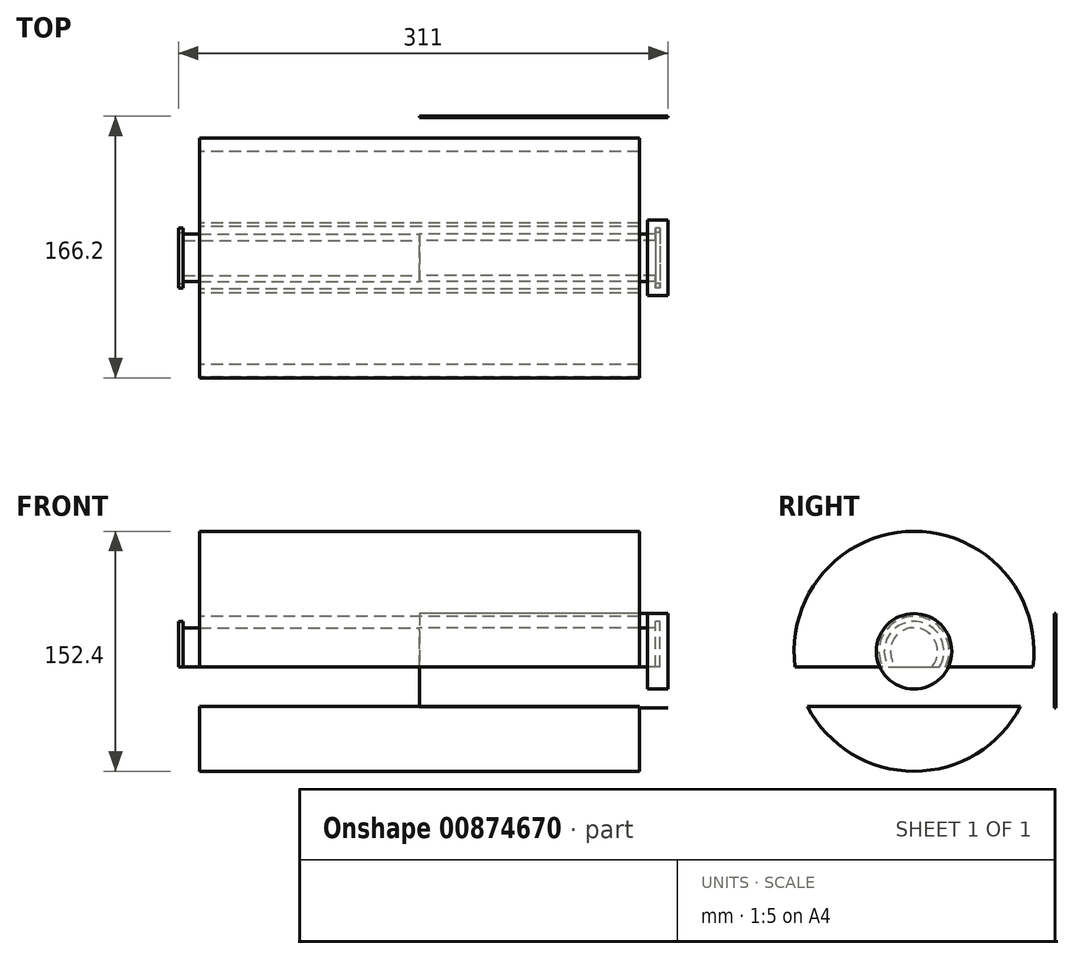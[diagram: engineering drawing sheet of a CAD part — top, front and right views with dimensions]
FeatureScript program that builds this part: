
annotation { "Feature Type Name" : "Feature", "Feature Type Description" : "" }
export const myFeature = defineFeature(function(context is Context, id is Id, definition is map)
    precondition{}
    {
        {
            var Q0;
            Q0=qCreatedBy(makeId("Right.planeOp"),FACE);
            var sketch = newSketch(context, id + "F0", { "sketchPlane" : qUnion([Q0])});
            skCircle(sketch, "E0", {"center": v(0, 0) * mm, "radius": 76.2 * mm});
            skCircle(sketch, "E1", {"center": v(0, 0) * mm, "radius": 22.23 * mm});
            skCircle(sketch, "E2", {"center": v(0, 0) * mm, "radius": 15 * mm});
            skCircle(sketch, "E3", {"center": v(0, 0) * mm, "radius": 19 * mm});
            skPoint(sketch, "E4", {"position": v(-19, 0) * mm});
            skPoint(sketch, "E5", {"position": v(-15, 0) * mm});
            skPoint(sketch, "E6", {"position": v(-22.23, 0) * mm});
            skPoint(sketch, "E7", {"position": v(15, 0) * mm});
            skPoint(sketch, "E8", {"position": v(19, 0) * mm});
            skPoint(sketch, "E9", {"position": v(22.23, 0) * mm});
            skPoint(sketch, "E10", {"position": v(0, 15) * mm});
            skPoint(sketch, "E11", {"position": v(0, 19) * mm});
            skPoint(sketch, "E12", {"position": v(0, 22.23) * mm});
            skPoint(sketch, "E13", {"position": v(0, -15) * mm});
            skPoint(sketch, "E14", {"position": v(0, -19) * mm});
            skPoint(sketch, "E15", {"position": v(0, -22.23) * mm});
            skSolve(sketch);
        }
        {
            var Q0;
            Q0=makeQuery(id+"F0.imprint","IMPRINT",FACE,{"disambiguationData":[TD([[makeQuery(id+"F0.imprint","IMPRINT",EDGE,{"derivedFrom":sQuery(id+"F0.wireOp",EDGE,"E0")}),1.0]])]});
            extrude(context, id + "F1", {"entities" : qUnion([Q0]), "endBound" : BoundingType.SYMMETRIC, "depth" : 279.4 * mm, "offsetDistance" : 25 * mm});
        }
        {
            var Q0;
            Q0=makeQuery(id+"F0.imprint","IMPRINT",FACE,{"disambiguationData":[TD([[makeQuery(id+"F0.imprint","IMPRINT",EDGE,{"derivedFrom":sQuery(id+"F0.wireOp",EDGE,"E2")}),1.0]])]});
            extrude(context, id + "F2", {"entities" : qUnion([Q0]), "depth" : 150 * mm, "offsetDistance" : 25 * mm});
        }
        {
            var Q0;
            Q0=makeQuery(id+"F0.imprint","IMPRINT",FACE,{"disambiguationData":[TD([[makeQuery(id+"F0.imprint","IMPRINT",EDGE,{"derivedFrom":sQuery(id+"F0.wireOp",EDGE,"E2")}),-1.0]])]});
            var Q1;
            Q1=makeQuery(id+"F0.imprint","IMPRINT",FACE,{"disambiguationData":[TD([[makeQuery(id+"F0.imprint","IMPRINT",EDGE,{"derivedFrom":sQuery(id+"F0.wireOp",EDGE,"E2")}),1.0]])]});
            var Q2;
            Q2=makeQuery(id+"F2.opExtrude","CAP_FACE",FACE,{"disambiguationData":[OSD([sQuery(id+"F0.wireOp",EDGE,"E2")])],"isStart":false});
            var Q3;
            Q3=makeQuery(id+"F2.opExtrude","CAP_FACE",FACE,{"disambiguationData":[OSD([sQuery(id+"F0.wireOp",EDGE,"E2")])],"isStart":false});
            extrude(context, id + "F3", {"entities" : qUnion([Q0, Q1]), "operationType" : NewBodyOperationType.ADD, "endBound" : BoundingType.UP_TO_SURFACE, "depth" : 25 * mm, "endBoundEntityFace" : qUnion([Q2]), "hasOffset" : true, "offsetDistance" : 3 * mm, "offsetOppositeDirection" : true, "hasSecondDirection" : true, "secondDirectionBound" : SecondDirectionBoundingType.UP_TO_SURFACE, "secondDirectionOppositeDirection" : false, "secondDirectionDepth" : 25 * mm, "secondDirectionBoundEntityFace" : qUnion([Q3])});
        }
        {
            var Q0;
            Q0=makeQuery(id+"F2.opExtrude","SWEPT_BODY",BODY,{"disambiguationData":[OSD([sQuery(id+"F0.wireOp",EDGE,"E2")])]});
            var Q1;
            Q1=makeQuery(id+"F0.imprint","IMPRINT",FACE,{"disambiguationData":[TD([[makeQuery(id+"F0.imprint","IMPRINT",EDGE,{"derivedFrom":sQuery(id+"F0.wireOp",EDGE,"E2")}),1.0]])]});
            mirror(context, id + "F4", {"operationType" : NewBodyOperationType.ADD, "entities" : qUnion([Q0]), "mirrorPlane" : qUnion([Q1])});
        }
        {
            var Q0;
            Q0=qCreatedBy(makeId("Top.planeOp"),FACE);
            cPlane(context, id + "F5", {"entities" : qUnion([Q0]), "cplaneType" : CPlaneType.OFFSET, "offset" : 10 * mm, "oppositeDirection" : true, "width" : 150 * mm, "height" : 150 * mm});
        }
        {
            var Q0;
            Q0=qCreatedBy(id+"F5.planeOp",FACE);
            var sketch = newSketch(context, id + "F6", { "sketchPlane" : qUnion([Q0])});
            skLineSegment(sketch, "E16.bottom", {"start": v(215.89, -121.03) * mm, "end": v(-215.89, -121.03) * mm});
            skLineSegment(sketch, "E16.top", {"start": v(215.89, 160.12) * mm, "end": v(-215.89, 160.12) * mm});
            skLineSegment(sketch, "E16.left", {"start": v(215.89, -121.03) * mm, "end": v(215.89, 160.12) * mm});
            skLineSegment(sketch, "E16.right", {"start": v(-215.89, -121.03) * mm, "end": v(-215.89, 160.12) * mm});
            skPoint(sketch, "E16.middle", {"position": v(0, 19.54) * mm});
            skSolve(sketch);
        }
        {
            var Q0;
            Q0=makeQuery(id+"F6.imprint","IMPRINT",FACE,{"disambiguationData":[TD([[makeQuery(id+"F6.imprint","IMPRINT",EDGE,{"derivedFrom":sQuery(id+"F6.wireOp",EDGE,"E16.bottom")}),-1.0]])]});
            extrude(context, id + "F7", {"entities" : qUnion([Q0]), "operationType" : NewBodyOperationType.REMOVE, "oppositeDirection" : true, "depth" : 25 * mm, "offsetDistance" : 25 * mm});
        }
        {
            var Q0;
            Q0=qCreatedBy(makeId("Front.planeOp"),FACE);
            cPlane(context, id + "F8", {"entities" : qUnion([Q0]), "cplaneType" : CPlaneType.OFFSET, "offset" : 90 * mm, "oppositeDirection" : true, "width" : 150 * mm, "height" : 150 * mm});
        }
        {
            var Q0;
            Q0=qCreatedBy(id+"F8.planeOp",FACE);
            var sketch = newSketch(context, id + "F9", { "sketchPlane" : qUnion([Q0])});
            skLineSegment(sketch, "E17", {"start": v(150, 19) * mm, "end": v(153, 19) * mm});
            skLineSegment(sketch, "E18.0", {"start": v(153, -10) * mm, "end": v(150, -10) * mm});
            skLineSegment(sketch, "E19.0", {"start": v(150, -10) * mm, "end": v(150, 19) * mm});
            skLineSegment(sketch, "E20.0", {"start": v(153, -10) * mm, "end": v(153, 19) * mm});
            skLineSegment(sketch, "E21.bottom", {"start": v(158, 24) * mm, "end": v(0, 24) * mm});
            skLineSegment(sketch, "E21.top", {"start": v(158, -36) * mm, "end": v(0, -36) * mm});
            skLineSegment(sketch, "E21.left", {"start": v(158, 24) * mm, "end": v(158, -36) * mm});
            skPoint(sketch, "E22", {"position": v(0, 24) * mm});
            skPoint(sketch, "E23.orphan", {"position": v(-158, 24) * mm});
            skPoint(sketch, "E24.end.orphan", {"position": v(-158, -36) * mm});
            skLineSegment(sketch, "E25", {"start": v(0, 24) * mm, "end": v(0, -36) * mm});
            skLineSegment(sketch, "E26", {"start": v(145, 24) * mm, "end": v(145, -36) * mm});
            skSolve(sketch);
        }
        {
            var Q0;
            Q0=makeQuery(id+"F9.imprint","IMPRINT",FACE,{"disambiguationData":[TD([[makeQuery(id+"F9.imprint","IMPRINT",EDGE,{"derivedFrom":sQuery(id+"F9.wireOp",EDGE,"E17")}),1.0]])]});
            var Q1;
            Q1=makeQuery(id+"F9.imprint","IMPRINT",FACE,{"disambiguationData":[TD([[makeQuery(id+"F9.imprint","IMPRINT",EDGE,{"derivedFrom":sQuery(id+"F9.wireOp",EDGE,"E17")}),-1.0]])]});
            var Q2;
            {var subQ0=sQuery(id+"F9.wireOp",EDGE,"E25");Q2=makeQuery(id+"F9.imprint","IMPRINT",FACE,{"disambiguationData":[TD([[makeQuery(id+"F9.imprint","IMPRINT",EDGE,{"derivedFrom":subQ0}),1.0]])]});}
            extrude(context, id + "F10", {"entities" : qUnion([Q0, Q1, Q2]), "depth" : 1 * mm, "offsetDistance" : 25 * mm});
        }
        {
            var Q0;
            Q0=makeQuery(id+"F3.opExtrude","CAP_FACE",FACE,{"disambiguationData":[OSD([sQuery(id+"F0.wireOp",EDGE,"E3")])],"isStart":false});
            var sketch = newSketch(context, id + "F11", { "sketchPlane" : qUnion([Q0])});
            skArc(sketch, "E27.0", {"start": v(16.16, -10) * mm, "mid": v(0, 19) * mm, "end": v(-16.16, -10) * mm});
            skCircle(sketch, "E28", {"center": v(0, 0) * mm, "radius": 24 * mm});
            skPoint(sketch, "E29", {"position": v(-19, 0) * mm});
            skPoint(sketch, "E30", {"position": v(-24, 0) * mm});
            skSolve(sketch);
        }
        {
            var Q0;
            Q0=makeQuery(id+"F11.imprint","IMPRINT",FACE,{"disambiguationData":[TD([[makeQuery(id+"F11.imprint","IMPRINT",EDGE,{"derivedFrom":sQuery(id+"F11.wireOp",EDGE,"E27.0")}),-1.0]])]});
            var Q1;
            Q1=makeQuery(id+"F11.imprint","IMPRINT",FACE,{"disambiguationData":[TD([[makeQuery(id+"F11.imprint","IMPRINT",EDGE,{"derivedFrom":sQuery(id+"F11.wireOp",EDGE,"E27.0")}),1.0]])]});
            var Q2;
            Q2=makeQuery(id+"F3.opExtrude","CAP_FACE",FACE,{"disambiguationData":[OSD([sQuery(id+"F0.wireOp",EDGE,"E3")])],"isStart":true});
            extrude(context, id + "F12", {"entities" : qUnion([Q0, Q1]), "depth" : 5 * mm, "offsetDistance" : 25 * mm, "hasSecondDirection" : true, "secondDirectionBound" : SecondDirectionBoundingType.UP_TO_SURFACE, "secondDirectionOppositeDirection" : true, "secondDirectionDepth" : 25 * mm, "secondDirectionBoundEntityFace" : qUnion([Q2]), "hasSecondDirectionOffset" : true, "secondDirectionOffsetDistance" : 5 * mm, "secondDirectionOffsetOppositeDirection" : true});
        }
    });
